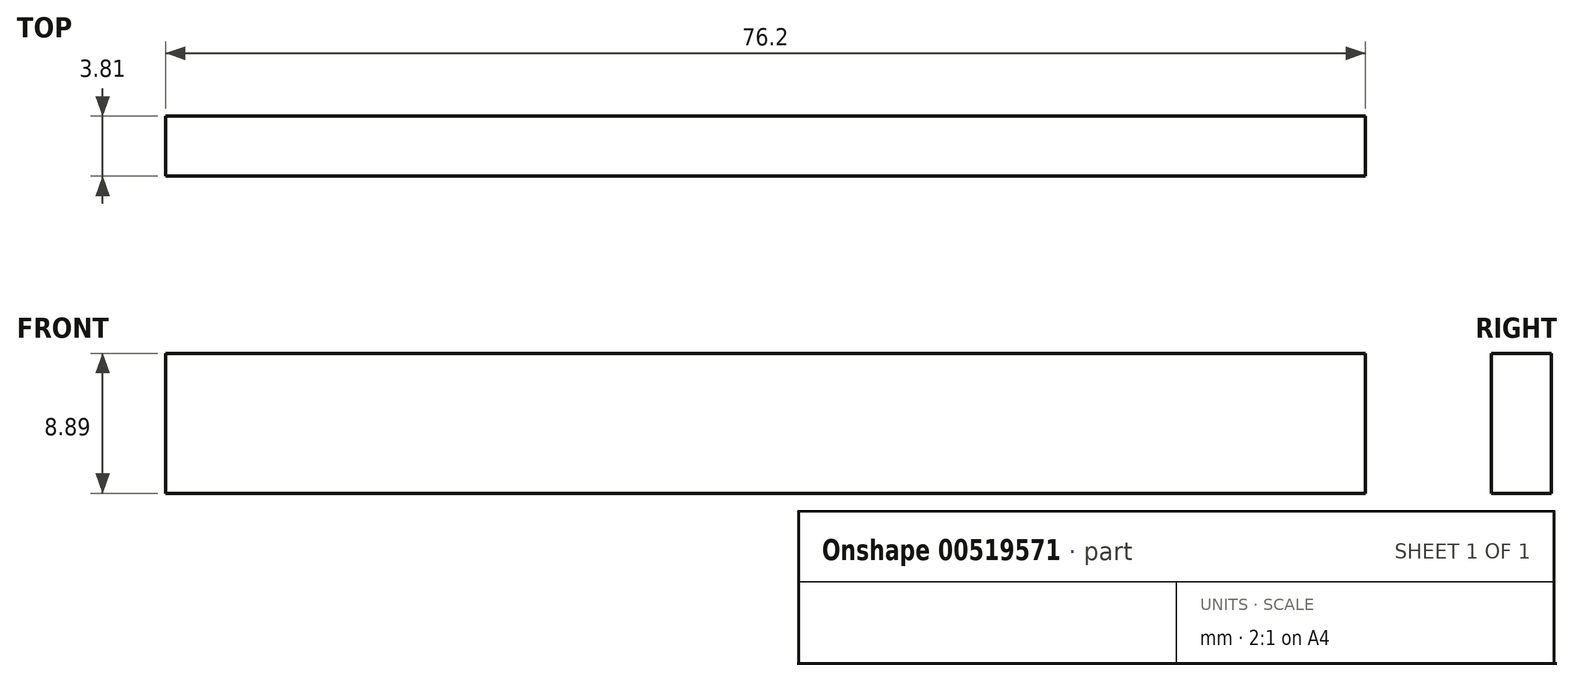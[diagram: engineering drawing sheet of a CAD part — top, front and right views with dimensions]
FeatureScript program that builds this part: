
annotation { "Feature Type Name" : "Feature", "Feature Type Description" : "" }
export const myFeature = defineFeature(function(context is Context, id is Id, definition is map)
    precondition{}
    {
        {
            var Q0;
            Q0=qCreatedBy(makeId("Top.planeOp"),FACE);
            var sketch = newSketch(context, id + "F0", { "sketchPlane" : qUnion([Q0])});
            skLineSegment(sketch, "E0.bottom", {"start": v(-25.27, 27.32) * mm, "end": v(50.93, 27.32) * mm});
            skLineSegment(sketch, "E0.top", {"start": v(-25.27, 23.5) * mm, "end": v(50.93, 23.5) * mm});
            skLineSegment(sketch, "E0.left", {"start": v(-25.27, 27.32) * mm, "end": v(-25.27, 23.5) * mm});
            skLineSegment(sketch, "E0.right", {"start": v(50.93, 27.32) * mm, "end": v(50.93, 23.5) * mm});
            skSolve(sketch);
        }
        {
            var Q0;
            Q0 = qSketchRegion(id + "F0", true);
            extrude(context, id + "F1", {"entities" : qUnion([Q0]), "depth" : 8.9 * mm, "offsetDistance" : 25.4 * mm});
        }
    });
